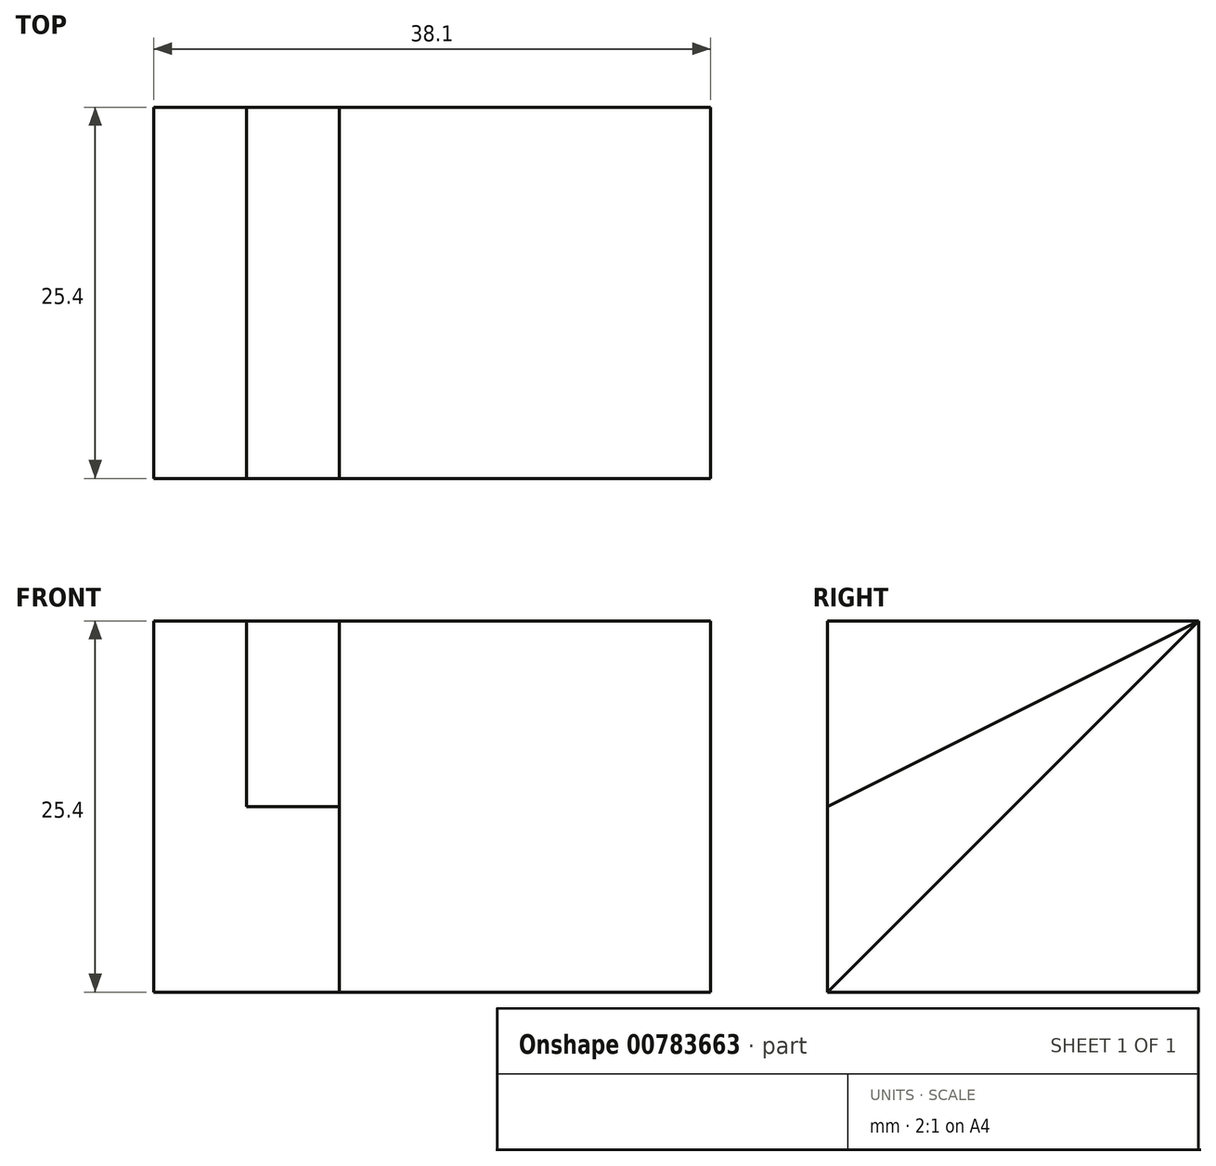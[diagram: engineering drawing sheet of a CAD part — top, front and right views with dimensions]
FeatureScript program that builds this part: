
annotation { "Feature Type Name" : "Feature", "Feature Type Description" : "" }
export const myFeature = defineFeature(function(context is Context, id is Id, definition is map)
    precondition{}
    {
        {
            var Q0;
            Q0=qCreatedBy(makeId("Front.planeOp"),FACE);
            var sketch = newSketch(context, id + "F0", { "sketchPlane" : qUnion([Q0])});
            skLineSegment(sketch, "E0", {"start": v(0, 0) * mm, "end": v(0, -25.4) * mm});
            skLineSegment(sketch, "E1", {"start": v(0, -25.4) * mm, "end": v(38.1, -25.4) * mm});
            skLineSegment(sketch, "E2", {"start": v(38.1, 0) * mm, "end": v(38.1, -25.4) * mm});
            skLineSegment(sketch, "E3", {"start": v(0, 0) * mm, "end": v(38.1, 0) * mm});
            skSolve(sketch);
        }
        {
            var Q0;
            Q0 = qSketchRegion(id + "F0", true);
            extrude(context, id + "F1", {"entities" : qUnion([Q0]), "depth" : 25.4 * mm, "offsetDistance" : 25.4 * mm});
        }
        {
            var Q0;
            Q0=makeQuery(id+"F1.opExtrude","SWEPT_FACE",FACE,{"disambiguationData":[OSD([sQuery(id+"F0.wireOp",EDGE,"E2")])]});
            var sketch = newSketch(context, id + "F2", { "sketchPlane" : qUnion([Q0])});
            skLineSegment(sketch, "E4", {"start": v(-25.4, -25.4) * mm, "end": v(0, 0) * mm});
            skSolve(sketch);
        }
        {
            var Q0;
            Q0 = qSketchRegion(id + "F2", true);
            var Q1;
            Q1=makeQuery(id+"F2.imprint","IMPRINT",FACE,{"disambiguationData":[TD([[makeQuery(id+"F2.imprint","IMPRINT",EDGE,{"derivedFrom":sQuery(id+"F2.wireOp",EDGE,"E4")}),1.0]])]});
            extrude(context, id + "F3", {"entities" : qUnion([Q0, Q1]), "operationType" : NewBodyOperationType.REMOVE, "oppositeDirection" : true, "depth" : 25.4 * mm, "offsetDistance" : 25.4 * mm});
        }
        {
            var Q0;
            Q0=makeQuery(id+"F3.boolean.opBoolean","COPY",FACE,{"derivedFrom":makeQuery(id+"F3.opExtrude","CAP_FACE",FACE,{"disambiguationData":[OSD([sQuery(id+"F0.wireOp",EDGE,"E2"),sQuery(id+"F0.wireOp",EDGE,"E3"),sQuery(id+"F2.wireOp",EDGE,"E4")])],"isStart":false})});
            var sketch = newSketch(context, id + "F4", { "sketchPlane" : qUnion([Q0])});
            skLineSegment(sketch, "E5", {"start": v(-25.4, 0) * mm, "end": v(-25.4, -12.7) * mm});
            skLineSegment(sketch, "E6", {"start": v(-25.4, -12.7) * mm, "end": v(0, 0) * mm});
            skSolve(sketch);
        }
        {
            var Q0;
            Q0 = qSketchRegion(id + "F4", true);
            var Q1;
            Q1=makeQuery(id+"F4.imprint","IMPRINT",FACE,{"disambiguationData":[TD([[makeQuery(id+"F4.imprint","IMPRINT",EDGE,{"derivedFrom":sQuery(id+"F4.wireOp",EDGE,"E5")}),1.0]])]});
            extrude(context, id + "F5", {"entities" : qUnion([Q0, Q1]), "operationType" : NewBodyOperationType.REMOVE, "oppositeDirection" : true, "depth" : 6.35 * mm, "offsetDistance" : 25.4 * mm});
        }
    });
